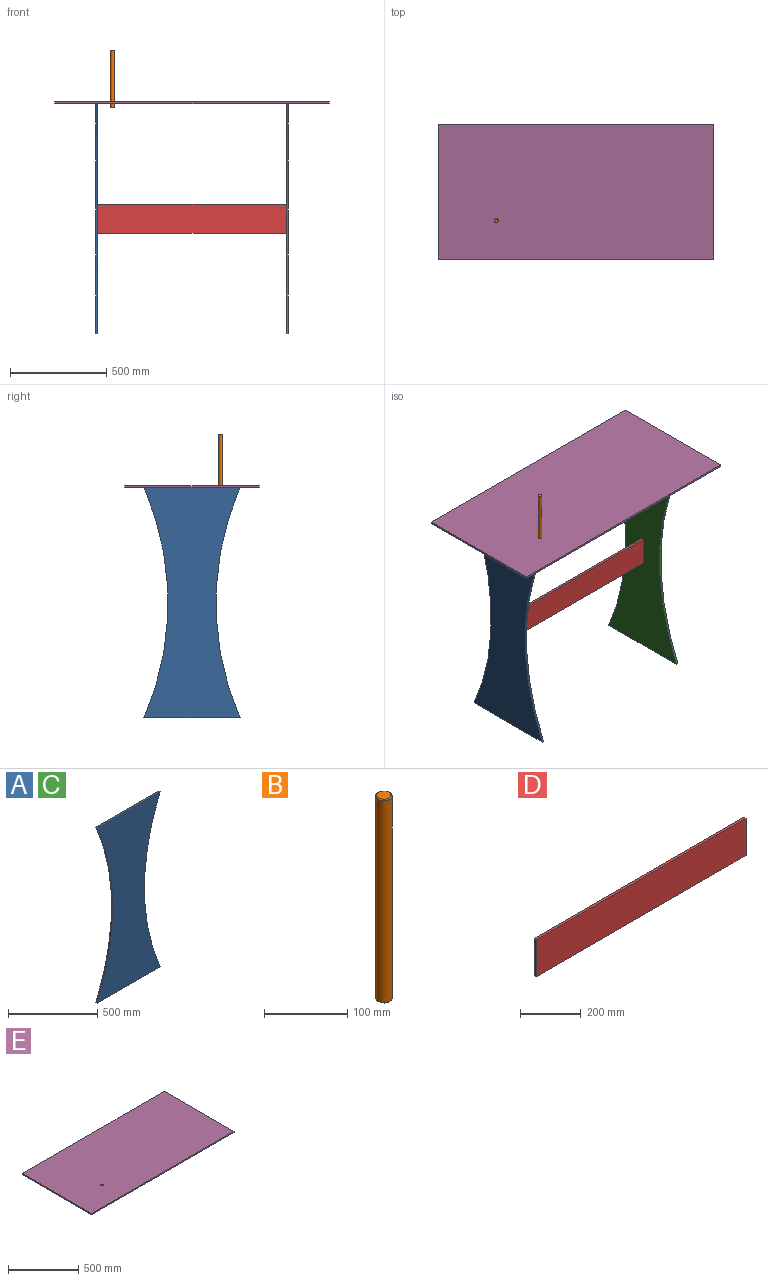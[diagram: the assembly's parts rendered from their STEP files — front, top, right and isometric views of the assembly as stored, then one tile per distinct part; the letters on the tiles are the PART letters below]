
ASSEMBLY  parts=5 mates=4
PART A: 6 faces, bbox 500x10x1200 mm
  f0: cylinder r=1500mm len=1200mm, axis (0,1,0), area 12345.5mm2, adj f1,f3,f4,f5
  f1: plane 500x10mm, normal (0,0,1), area 5000mm2, adj f0,f2,f4,f5
  f2: cylinder r=1500mm len=1200mm, axis (0,1,0), area 12345.5mm2, adj f1,f3,f4,f5
  f3: plane 500x10mm, normal (0,0,-1), area 5000mm2, adj f0,f2,f4,f5
  f4: plane 1200x500mm, normal (0,-1,0), area 397901.4mm2, adj f0,f1,f2,f3
  f5: plane 1200x500mm, normal (0,1,0), area 397901.4mm2, adj f0,f1,f2,f3
PART B: 5 faces, bbox 20x20x300 mm
  f0: cylinder r=10mm len=297mm, axis (0,0,-1), area 18661.1mm2, adj f3,f4
  f1: plane 17x17mm, normal (0,0,1), area 227mm2, adj f4
  f2: plane 17x17mm, normal (0,0,-1), area 227mm2, adj f3
  f3: cone r=10mm half-angle=45deg, axis (0,0,1), area 123.3mm2, adj f0,f2
  f4: cone r=8.5mm half-angle=45deg, axis (0,0,-1), area 123.3mm2, adj f0,f1
PART C: same geometry as A
PART D: 6 faces, bbox 980x10x150 mm
  f0: plane 150x10mm, normal (1,0,0), area 1500mm2, adj f1,f3,f4,f5
  f1: plane 980x10mm, normal (0,0,1), area 9800mm2, adj f0,f2,f4,f5
  f2: plane 150x10mm, normal (-1,0,0), area 1500mm2, adj f1,f3,f4,f5
  f3: plane 980x10mm, normal (0,0,-1), area 9800mm2, adj f0,f2,f4,f5
  f4: plane 980x150mm, normal (0,-1,0), area 147000mm2, adj f0,f1,f2,f3
  f5: plane 980x150mm, normal (0,1,0), area 147000mm2, adj f0,f1,f2,f3
PART E: 7 faces, bbox 1430x700x10 mm
  f0: plane 1430x10mm, normal (0,-1,0), area 14300mm2, adj f1,f4,f5,f6
  f1: plane 700x10mm, normal (1,0,0), area 7000mm2, adj f0,f2,f5,f6
  f2: plane 1430x10mm, normal (0,1,0), area 14300mm2, adj f1,f4,f5,f6
  f3: cylinder r=10mm len=20mm, axis (0,0,-1), area 628.3mm2, adj f5,f6
  f4: plane 700x10mm, normal (-1,0,0), area 7000mm2, adj f0,f2,f5,f6
  f5: plane 1430x700mm, normal (0,0,1), area 1000685.8mm2, adj f0,f1,f2,f3,f4
  f6: plane 1430x700mm, normal (0,0,-1), area 1000685.8mm2, adj f0,f1,f2,f3,f4
PLACE A rot(axis=(0,0,-1),90deg) t=(78.6,-1249.24,-132.74)mm
PLACE B t=(1252.92,-321.11,125.88)mm
PLACE C rot(axis=(0,0,-1),90deg) t=(1068.6,-1249.24,-132.74)mm
PLACE D t=(1574.67,192.94,-1423.66)mm
PLACE E t=(568.6,187.94,147.38)mm
MATE fastened B.f0 <-> E.f3  axis (0,0,-1) through (153.6,37.94,127.38)mm
MATE fastened C.f1 <-> E.f6  axis (0,0,1) through (1063.6,187.94,147.38)mm
MATE fastened D.f2 <-> A.f5  axis (-1,0,0) through (78.6,187.94,-452.62)mm
MATE fastened A.f1 <-> E.f6  axis (0,0,1) through (73.6,187.94,147.38)mm
